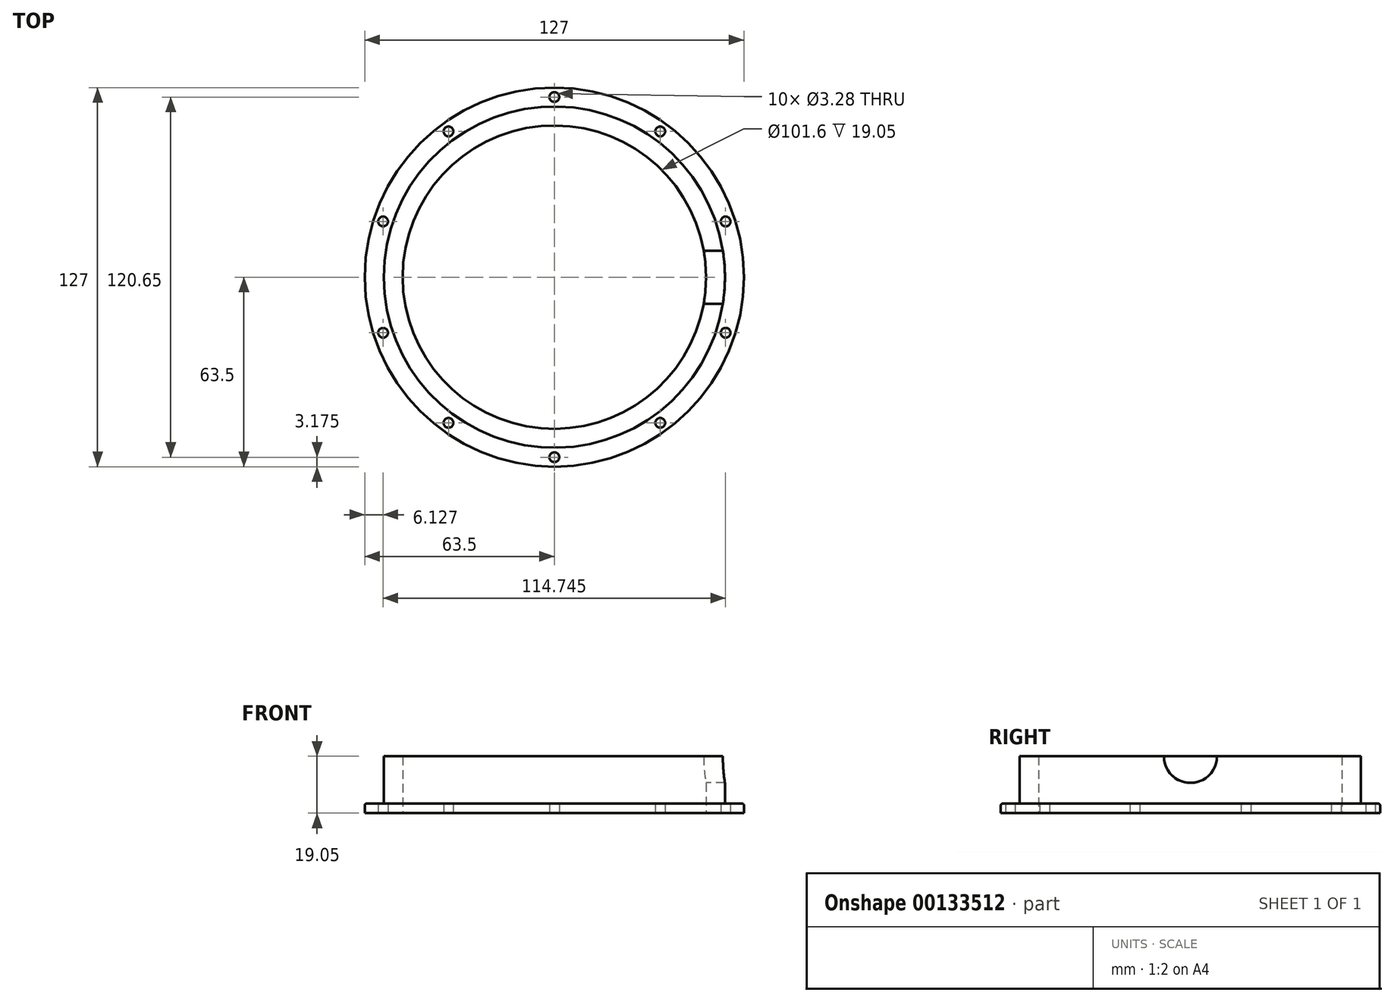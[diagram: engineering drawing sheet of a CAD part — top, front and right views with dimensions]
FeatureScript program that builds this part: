
annotation { "Feature Type Name" : "Feature", "Feature Type Description" : "" }
export const myFeature = defineFeature(function(context is Context, id is Id, definition is map)
    precondition{}
    {
        {
            var Q0;
            Q0=qCreatedBy(makeId("Top.planeOp"),FACE);
            var sketch = newSketch(context, id + "F0", { "sketchPlane" : qUnion([Q0])});
            skCircle(sketch, "E0", {"center": v(0, 0) * mm, "radius": 63.5 * mm});
            skSolve(sketch);
        }
        {
            var Q0;
            Q0=qSketchRegion(id+"F0",true);
            extrude(context, id + "F1", {"entities" : qUnion([Q0]), "depth" : 3.17 * mm});
        }
        {
            var Q0;
            Q0=qCreatedBy(makeId("Top.planeOp"),FACE);
            var sketch = newSketch(context, id + "F2", { "sketchPlane" : qUnion([Q0])});
            skCircle(sketch, "E1", {"center": v(0, 0) * mm, "radius": 57.15 * mm});
            skSolve(sketch);
        }
        {
            var Q0;
            Q0=qSketchRegion(id+"F2",true);
            extrude(context, id + "F3", {"entities" : qUnion([Q0]), "operationType" : NewBodyOperationType.ADD, "depth" : 58.74 * mm});
        }
        {
            var Q0;
            Q0=makeQuery(id+"F1.opExtrude","CAP_FACE",FACE,{"disambiguationData":[OSD([sQuery(id+"F0.wireOp",EDGE,"E0")])],"isStart":true});
            var sketch = newSketch(context, id + "F4", { "sketchPlane" : qUnion([Q0])});
            skCircle(sketch, "E2", {"center": v(0, 0) * mm, "radius": 50.8 * mm});
            skSolve(sketch);
        }
        {
            var Q0;
            Q0=qSketchRegion(id+"F4",true);
            extrude(context, id + "F5", {"entities" : qUnion([Q0]), "operationType" : NewBodyOperationType.REMOVE, "oppositeDirection" : true, "depth" : 50.8 * mm});
        }
        {
            var Q0;
            Q0=makeQuery(id+"F1.opExtrude","CAP_FACE",FACE,{"disambiguationData":[OSD([sQuery(id+"F0.wireOp",EDGE,"E0")])],"isStart":true});
            var sketch = newSketch(context, id + "F6", { "sketchPlane" : qUnion([Q0])});
            skCircle(sketch, "E3", {"center": v(0, -60.33) * mm, "radius": 1.64 * mm});
            skCircle(sketch, "E4.1.0", {"center": v(35.46, -48.8) * mm, "radius": 1.64 * mm});
            skCircle(sketch, "E4.2.0", {"center": v(57.37, -18.64) * mm, "radius": 1.64 * mm});
            skCircle(sketch, "E4.3.0", {"center": v(57.37, 18.64) * mm, "radius": 1.64 * mm});
            skCircle(sketch, "E4.4.0", {"center": v(35.46, 48.8) * mm, "radius": 1.64 * mm});
            skCircle(sketch, "E4.5.0", {"center": v(0, 60.33) * mm, "radius": 1.64 * mm});
            skCircle(sketch, "E4.6.0", {"center": v(-35.46, 48.8) * mm, "radius": 1.64 * mm});
            skCircle(sketch, "E4.7.0", {"center": v(-57.37, 18.64) * mm, "radius": 1.64 * mm});
            skCircle(sketch, "E4.8.0", {"center": v(-57.37, -18.64) * mm, "radius": 1.64 * mm});
            skCircle(sketch, "E4.9.0", {"center": v(-35.46, -48.8) * mm, "radius": 1.64 * mm});
            skPoint(sketch, "E4.center", {"position": v(0, 0) * mm});
            skSolve(sketch);
        }
        {
            var Q0;
            Q0=qSketchRegion(id+"F6",true);
            extrude(context, id + "F7", {"entities" : qUnion([Q0]), "operationType" : NewBodyOperationType.REMOVE, "endBound" : BoundingType.UP_TO_NEXT, "oppositeDirection" : true, "depth" : 25.4 * mm});
        }
        {
            var Q0;
            Q0=makeQuery(id+"F5.boolean.opBoolean","COPY",FACE,{"derivedFrom":makeQuery(id+"F5.opExtrude","CAP_FACE",FACE,{"disambiguationData":[OSD([sQuery(id+"F4.wireOp",EDGE,"E2")])],"isStart":false})});
            var sketch = newSketch(context, id + "F8", { "sketchPlane" : qUnion([Q0])});
            skLineSegment(sketch, "E5.bottom", {"start": v(-31.12, 31.12) * mm, "end": v(31.12, 31.12) * mm, "construction": true});
            skLineSegment(sketch, "E5.top", {"start": v(-31.12, -31.12) * mm, "end": v(31.11, -31.12) * mm, "construction": true});
            skLineSegment(sketch, "E5.left", {"start": v(-31.11, 31.12) * mm, "end": v(-31.12, -31.12) * mm, "construction": true});
            skLineSegment(sketch, "E5.right", {"start": v(31.12, 31.12) * mm, "end": v(31.11, -31.12) * mm, "construction": true});
            skPoint(sketch, "E5.middle", {"position": v(0, 0) * mm});
            skCircle(sketch, "E6", {"center": v(31.11, -31.12) * mm, "radius": 1.13 * mm});
            skCircle(sketch, "E7", {"center": v(-31.12, -31.12) * mm, "radius": 1.13 * mm});
            skCircle(sketch, "E8", {"center": v(-31.12, 31.12) * mm, "radius": 1.13 * mm});
            skCircle(sketch, "E9", {"center": v(31.12, 31.12) * mm, "radius": 1.13 * mm});
            skCircle(sketch, "E10", {"center": v(31.12, 0) * mm, "radius": 1.13 * mm});
            skCircle(sketch, "E11", {"center": v(-31.12, 0) * mm, "radius": 1.13 * mm});
            skSolve(sketch);
        }
        {
            var Q0;
            Q0=qSketchRegion(id+"F8",true);
            extrude(context, id + "F9", {"entities" : qUnion([Q0]), "operationType" : NewBodyOperationType.REMOVE, "oppositeDirection" : true, "depth" : 5.56 * mm});
        }
        {
            var Q0;
            Q0=qCreatedBy(makeId("Right.planeOp"),FACE);
            var sketch = newSketch(context, id + "F10", { "sketchPlane" : qUnion([Q0])});
            skCircle(sketch, "E12", {"center": v(0, 19.05) * mm, "radius": 8.9 * mm});
            skSolve(sketch);
        }
        {
            var Q0;
            Q0=qSketchRegion(id+"F10",true);
            var Q1;
            Q1=makeQuery(id+"F3.opExtrude","SWEPT_FACE",FACE,{"disambiguationData":[OSD([sQuery(id+"F2.wireOp",EDGE,"E1")])]});
            extrude(context, id + "F11", {"entities" : qUnion([Q0]), "operationType" : NewBodyOperationType.REMOVE, "endBound" : BoundingType.UP_TO_SURFACE, "endBoundEntityFace" : qUnion([Q1]), "depth" : 25.4 * mm});
        }
        {
            var Q0;
            Q0=makeQuery(id+"F3.opExtrude","CAP_EDGE",EDGE,{"disambiguationData":[OSD([sQuery(id+"F2.wireOp",EDGE,"E1")])],"isStart":false});
            var Q1;
            Q1=makeQuery(id+"F1.opExtrude","CAP_EDGE",EDGE,{"disambiguationData":[OSD([sQuery(id+"F0.wireOp",EDGE,"E0")])],"isStart":false});
            var Q2;
            {var subQ0=sQuery(id+"F2.wireOp",EDGE,"E1");Q2=makeQuery(id+"F11.boolean.opBoolean","INTERSECT",EDGE,{"derivedFrom":[makeQuery(id+"FComq4A4aaWOkHa_1.opShell","OFFSET_FACE",FACE,{"disambiguationData":[OSD([subQ0]),TDD([makeQuery(id+"F3.opExtrude","SWEPT_FACE",FACE,{"disambiguationData":[OSD([subQ0])]})])]}),makeQuery(id+"F11.opExtrude","SWEPT_FACE",FACE,{"disambiguationData":[OSD([sQuery(id+"F10.wireOp",EDGE,"E12")])]})]});}
            var Q3;
            Q3=makeQuery(id+"F3.boolean.opBoolean","INTERSECT",EDGE,{"derivedFrom":[makeQuery(id+"F1.opExtrude","CAP_FACE",FACE,{"disambiguationData":[OSD([sQuery(id+"F0.wireOp",EDGE,"E0")])],"isStart":false}),makeQuery(id+"F3.opExtrude","SWEPT_FACE",FACE,{"disambiguationData":[OSD([sQuery(id+"F2.wireOp",EDGE,"E1")])]})]});
            fillet(context, id + "F12", {"entities" : qUnion([Q0, Q1, Q2, Q3]), "radius" : 0.5 * mm, "tangentPropagation" : true, "allowEdgeOverflow" : false});
        }
        {
            var Q0;
            Q0=qCreatedBy(makeId("Front.planeOp"),FACE);
            var sketch = newSketch(context, id + "F13", { "sketchPlane" : qUnion([Q0])});
            skLineSegment(sketch, "E13.bottom", {"start": v(69.85, 19.05) * mm, "end": v(-69.85, 19.05) * mm});
            skLineSegment(sketch, "E13.top", {"start": v(69.85, 69.85) * mm, "end": v(-69.85, 69.85) * mm});
            skLineSegment(sketch, "E13.left", {"start": v(69.85, 19.05) * mm, "end": v(69.85, 69.85) * mm});
            skLineSegment(sketch, "E13.right", {"start": v(-69.85, 19.05) * mm, "end": v(-69.85, 69.85) * mm});
            skPoint(sketch, "E13.middle", {"position": v(0, 44.45) * mm});
            skSolve(sketch);
        }
        {
            var Q0;
            Q0 = qSketchRegion(id + "F13", true);
            extrude(context, id + "F14", {"entities" : qUnion([Q0]), "operationType" : NewBodyOperationType.REMOVE, "endBound" : BoundingType.SYMMETRIC, "oppositeDirection" : true, "depth" : 127 * mm});
        }
    });
